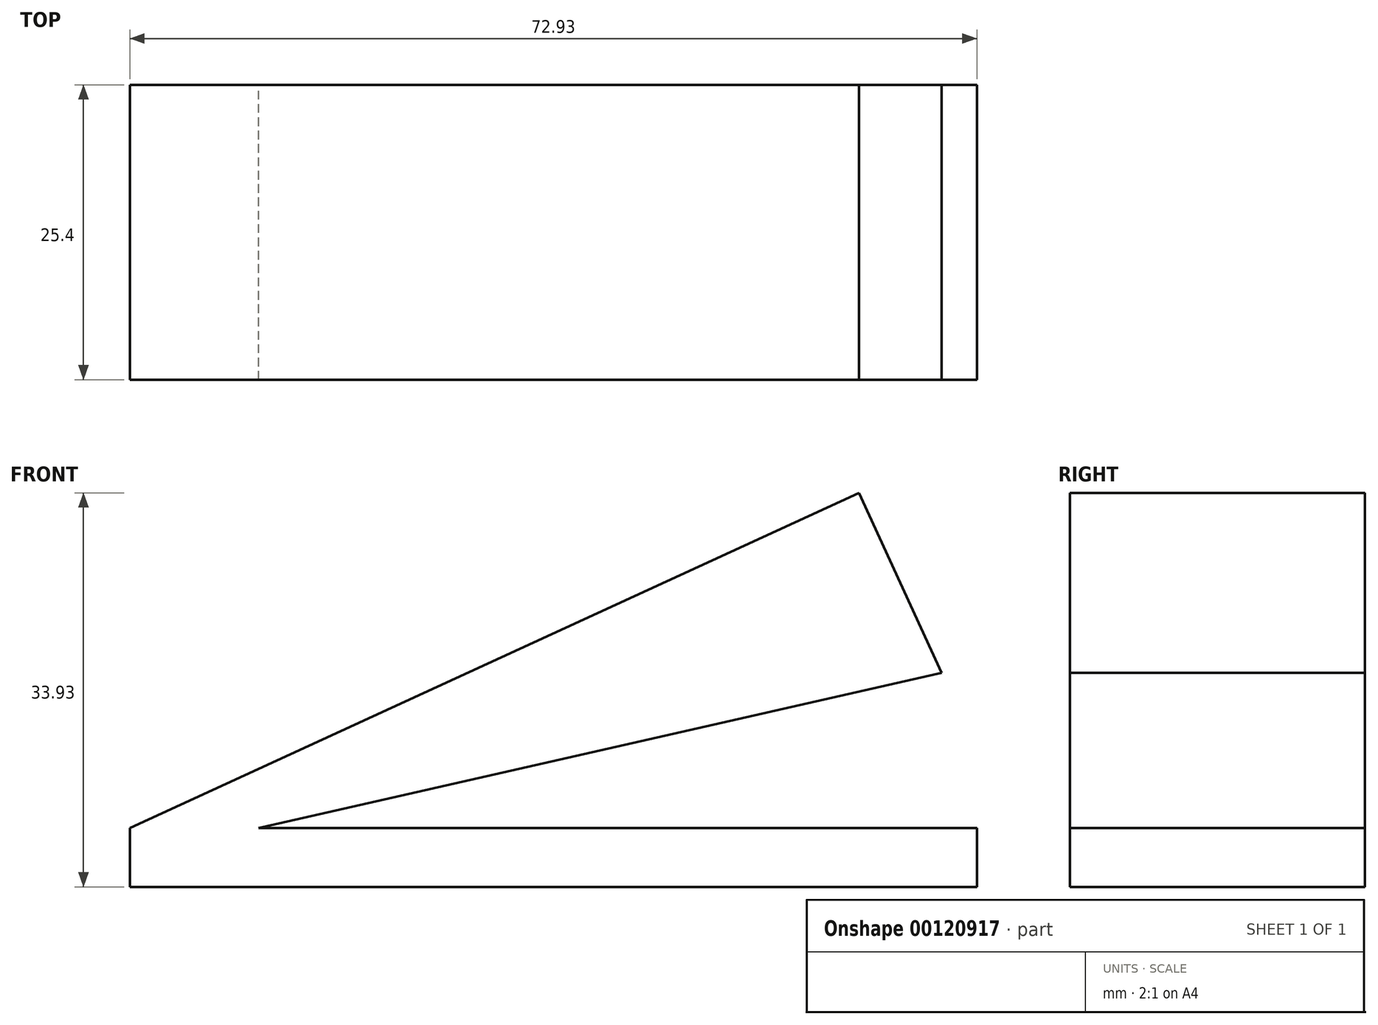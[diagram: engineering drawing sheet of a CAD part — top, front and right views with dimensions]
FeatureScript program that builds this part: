
annotation { "Feature Type Name" : "Feature", "Feature Type Description" : "" }
export const myFeature = defineFeature(function(context is Context, id is Id, definition is map)
    precondition{}
    {
        {
            var Q0;
            Q0=qCreatedBy(makeId("Front.planeOp"),FACE);
            var sketch = newSketch(context, id + "F0", { "sketchPlane" : qUnion([Q0])});
            skLineSegment(sketch, "E0.bottom", {"start": v(-35.54, -33.93) * mm, "end": v(37.39, -33.93) * mm});
            skLineSegment(sketch, "E0.top", {"start": v(-35.54, -28.85) * mm, "end": v(37.39, -28.85) * mm});
            skLineSegment(sketch, "E0.left", {"start": v(-35.54, -33.93) * mm, "end": v(-35.54, -28.85) * mm});
            skLineSegment(sketch, "E0.right", {"start": v(37.39, -33.93) * mm, "end": v(37.39, -28.85) * mm});
            skLineSegment(sketch, "E1", {"start": v(-35.54, -28.85) * mm, "end": v(27.23, 0) * mm});
            skLineSegment(sketch, "E2", {"start": v(27.23, 0) * mm, "end": v(34.35, -15.49) * mm});
            skLineSegment(sketch, "E3", {"start": v(34.35, -15.49) * mm, "end": v(-24.46, -28.85) * mm});
            skSolve(sketch);
        }
        {
            var Q0;
            {var subQ0=sQuery(id+"F0.wireOp",EDGE,"E1");Q0=makeQuery(id+"F0.imprint","IMPRINT",FACE,{"disambiguationData":[TD([[makeQuery(id+"F0.imprint","IMPRINT",EDGE,{"derivedFrom":subQ0}),-1.0]])]});}
            var Q1;
            Q1=makeQuery(id+"F0.imprint","IMPRINT",FACE,{"disambiguationData":[TD([[makeQuery(id+"F0.imprint","IMPRINT",EDGE,{"derivedFrom":sQuery(id+"F0.wireOp",EDGE,"E0.bottom")}),1.0]])]});
            extrude(context, id + "F1", {"entities" : qUnion([Q0, Q1]), "depth" : 25.4 * mm});
        }
    });
